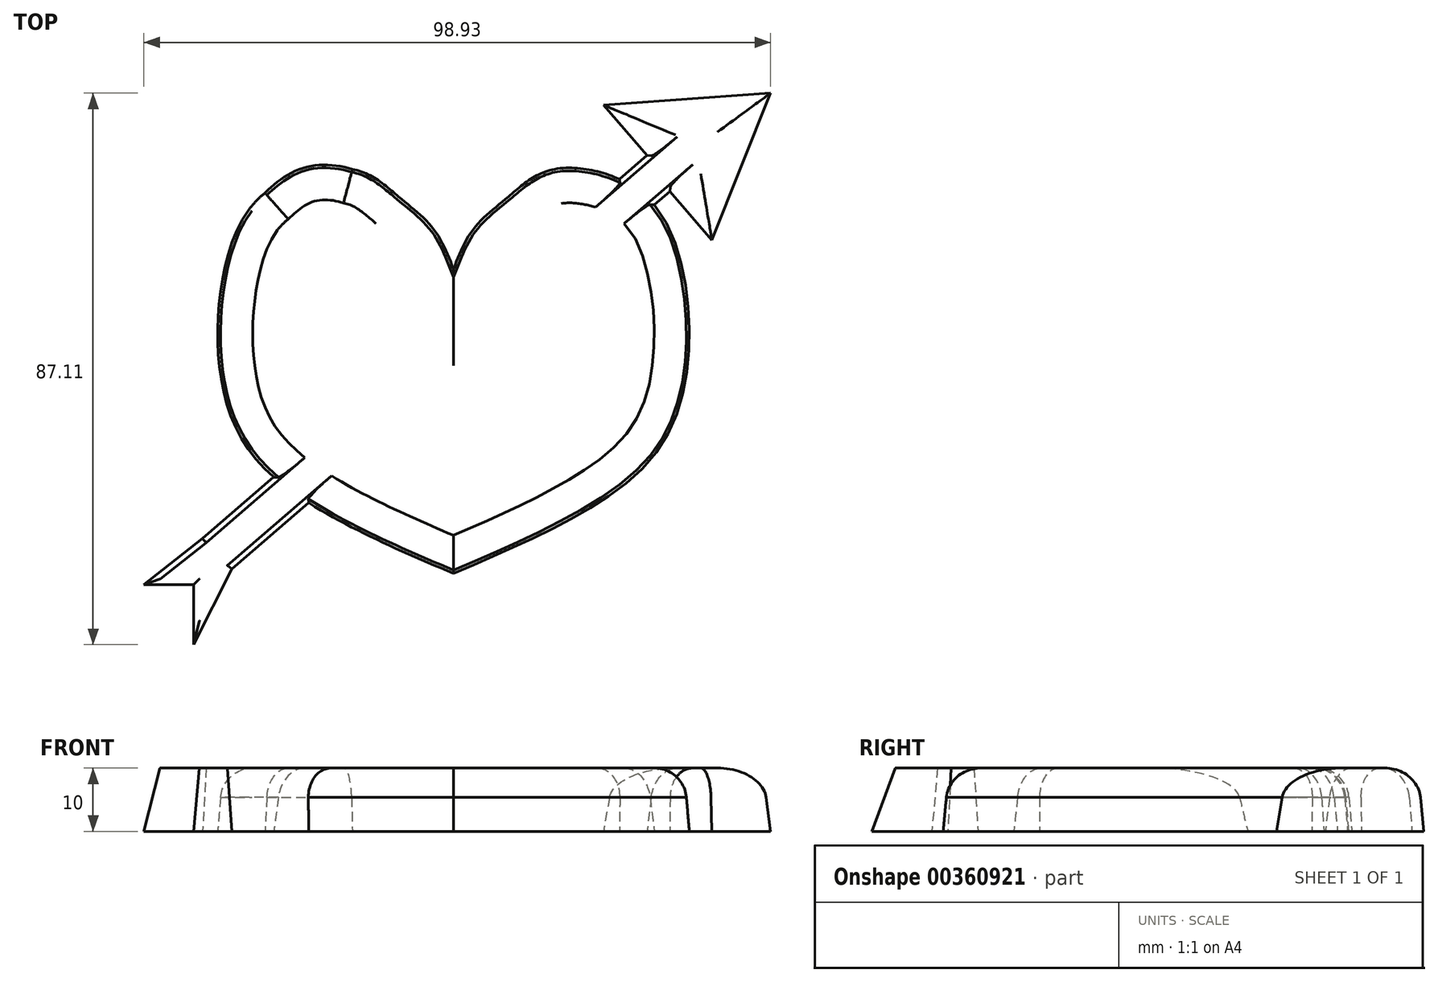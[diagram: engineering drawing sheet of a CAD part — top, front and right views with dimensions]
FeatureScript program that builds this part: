
annotation { "Feature Type Name" : "Feature", "Feature Type Description" : "" }
export const myFeature = defineFeature(function(context is Context, id is Id, definition is map)
    precondition{}
    {
        {
            var Q0;
            Q0=qCreatedBy(makeId("Top.planeOp"),FACE);
            var sketch = newSketch(context, id + "F0", { "sketchPlane" : qUnion([Q0])});
            skFitSpline(sketch, "E0", {"points": [v(0, -36.65) * mm, v(-17.54, -28.58) * mm, v(-31.73, -17.93) * mm, v(-36.85, -4.73) * mm, v(-36.26, 10.84) * mm, v(-29.76, 23.45) * mm, v(-15.96, 27.2) * mm, v(-8.67, 22.86) * mm, v(-3.15, 17.74) * mm, v(0, 11.43) * mm], "startDerivative": vector(-129.74, 55.22) * mm, "endDerivative": vector(31.5, -80.86) * mm});
            skFitSpline(sketch, "E1.MirrorCS", {"points": [v(0, -36.65) * mm, v(17.54, -28.58) * mm, v(31.73, -17.93) * mm, v(36.85, -4.73) * mm, v(36.26, 10.84) * mm, v(29.76, 23.45) * mm, v(15.96, 27.2) * mm, v(8.67, 22.86) * mm, v(3.15, 17.74) * mm, v(0, 11.43) * mm], "startDerivative": vector(129.74, 55.22) * mm, "endDerivative": vector(-31.5, -80.86) * mm});
            skLineSegment(sketch, "E2", {"start": v(-39.61, -31.14) * mm, "end": v(-28.37, -21.44) * mm});
            skLineSegment(sketch, "E3", {"start": v(30.55, 29.36) * mm, "end": v(23.67, 37.34) * mm});
            skLineSegment(sketch, "E4", {"start": v(23.67, 37.34) * mm, "end": v(50.06, 39.22) * mm});
            skLineSegment(sketch, "E5", {"start": v(50.06, 39.22) * mm, "end": v(40.8, 15.96) * mm});
            skLineSegment(sketch, "E6", {"start": v(40.8, 15.96) * mm, "end": v(34.15, 23.67) * mm});
            skLineSegment(sketch, "E7", {"start": v(34.15, 23.67) * mm, "end": v(31.7, 21.55) * mm});
            skLineSegment(sketch, "E8", {"start": v(-34.97, -35.93) * mm, "end": v(-41, -47.89) * mm});
            skLineSegment(sketch, "E9", {"start": v(-41, -47.89) * mm, "end": v(-41, -38.43) * mm});
            skLineSegment(sketch, "E10", {"start": v(-41, -38.43) * mm, "end": v(-48.87, -38.43) * mm});
            skLineSegment(sketch, "E11", {"start": v(-48.87, -38.43) * mm, "end": v(-39.61, -31.14) * mm});
            skLineSegment(sketch, "E12.trimOffspring", {"start": v(26.2, 25.62) * mm, "end": v(30.55, 29.36) * mm});
            skLineSegment(sketch, "E13.trimOffspring", {"start": v(-22.86, -25.5) * mm, "end": v(-34.97, -35.93) * mm});
            skFitSpline(sketch, "E14.trimOffspring", {"points": [v(0, -36.65) * mm, v(-17.54, -28.58) * mm, v(-31.73, -17.93) * mm, v(-36.85, -4.73) * mm, v(-36.26, 10.84) * mm, v(-29.76, 23.45) * mm, v(-15.96, 27.2) * mm, v(-8.67, 22.86) * mm, v(-3.15, 17.74) * mm, v(0, 11.43) * mm], "startDerivative": vector(-129.74, 55.22) * mm, "endDerivative": vector(31.5, -80.86) * mm});
            skPoint(sketch, "E15.start.orphan", {"position": v(15.77, 47.88) * mm});
            skPoint(sketch, "E16.end.orphan", {"position": v(-22.26, 47.88) * mm});
            skFitSpline(sketch, "E17", {"points": [v(-32.2, 20.93) * mm, v(-29.76, 23.45) * mm, v(-24.3, 27.2) * mm, v(-15.96, 27.2) * mm, v(-8.67, 22.86) * mm], "startDerivative": vector(11.95, 12.9) * mm, "endDerivative": vector(24.17, -18.2) * mm});
            skFitSpline(sketch, "E18", {"points": [v(8.67, 22.86) * mm, v(15.96, 27.2) * mm, v(26.2, 25.62) * mm], "startDerivative": vector(14.36, 12) * mm, "endDerivative": vector(20.6, -6.2) * mm});
            skSolve(sketch);
        }
        {
            var Q0;
            Q0 = qSketchRegion(id + "F0", true);
            extrude(context, id + "F1", {"entities" : qUnion([Q0]), "depth" : 10 * mm, "hasDraft" : true, "draftAngle" : 5 * degree, "draftPullDirection" : true});
        }
        {
            var Q0;
            Q0=makeQuery(id+"F1.opExtrude","CAP_EDGE",EDGE,{"disambiguationData":[OSD([sQuery(id+"F0.wireOp",EDGE,"E14.trimOffspring")])],"isStart":false});
            var Q1;
            Q1=makeQuery(id+"F1.opExtrude","CAP_EDGE",EDGE,{"disambiguationData":[OSD([sQuery(id+"F0.wireOp",EDGE,"E17")])],"isStart":false});
            var Q2;
            Q2=makeQuery(id+"F1.opExtrude","CAP_EDGE",EDGE,{"disambiguationData":[OSD([sQuery(id+"F0.wireOp",EDGE,"E0")])],"isStart":false});
            var Q3;
            Q3=makeQuery(id+"F1.opExtrude","CAP_EDGE",EDGE,{"disambiguationData":[OSD([sQuery(id+"F0.wireOp",EDGE,"E1.MirrorCS")])],"isStart":false});
            var Q4;
            Q4=makeQuery(id+"F1.opExtrude","CAP_EDGE",EDGE,{"disambiguationData":[OSD([sQuery(id+"F0.wireOp",EDGE,"E18")])],"isStart":false});
            var Q5;
            Q5=makeQuery(id+"F1.opExtrude","CAP_EDGE",EDGE,{"disambiguationData":[OSD([sQuery(id+"F0.wireOp",EDGE,"E1.MirrorCS")])],"isStart":false});
            var Q6;
            Q6=makeQuery(id+"F1.opExtrude","CAP_EDGE",EDGE,{"disambiguationData":[OSD([sQuery(id+"F0.wireOp",EDGE,"E0")])],"isStart":false});
            fillet(context, id + "F2", {"entities" : qUnion([Q0, Q1, Q2, Q3, Q4, Q5, Q6]), "radius" : 5.08 * mm, "tangentPropagation" : true, "allowEdgeOverflow" : false});
        }
        {
            var Q0;
            Q0=makeQuery(id+"F1.opExtrude","CAP_EDGE",EDGE,{"disambiguationData":[OSD([sQuery(id+"F0.wireOp",EDGE,"E5")])],"isStart":false});
            var Q1;
            Q1=makeQuery(id+"F1.opExtrude","CAP_EDGE",EDGE,{"disambiguationData":[OSD([sQuery(id+"F0.wireOp",EDGE,"E4")])],"isStart":false});
            var Q2;
            Q2=makeQuery(id+"F1.opExtrude","CAP_EDGE",EDGE,{"disambiguationData":[OSD([sQuery(id+"F0.wireOp",EDGE,"E3")])],"isStart":false});
            var Q3;
            Q3=makeQuery(id+"F1.opExtrude","CAP_EDGE",EDGE,{"disambiguationData":[OSD([sQuery(id+"F0.wireOp",EDGE,"E6")])],"isStart":false});
            fillet(context, id + "F3", {"entities" : qUnion([Q0, Q1, Q2, Q3]), "radius" : 5.08 * mm, "tangentPropagation" : true, "allowEdgeOverflow" : false});
        }
        {
            var Q0;
            Q0=makeQuery(id+"F1.opExtrude","CAP_EDGE",EDGE,{"disambiguationData":[OSD([sQuery(id+"F0.wireOp",EDGE,"E9")])],"isStart":false});
            var Q1;
            Q1=makeQuery(id+"F1.opExtrude","CAP_EDGE",EDGE,{"disambiguationData":[OSD([sQuery(id+"F0.wireOp",EDGE,"E10")])],"isStart":false});
            var Q2;
            Q2=makeQuery(id+"F1.opExtrude","CAP_EDGE",EDGE,{"disambiguationData":[OSD([sQuery(id+"F0.wireOp",EDGE,"E8")])],"isStart":false});
            fillet(context, id + "F4", {"entities" : qUnion([Q0, Q1, Q2]), "radius" : 0.03 * mm, "tangentPropagation" : true, "allowEdgeOverflow" : false});
        }
    });
